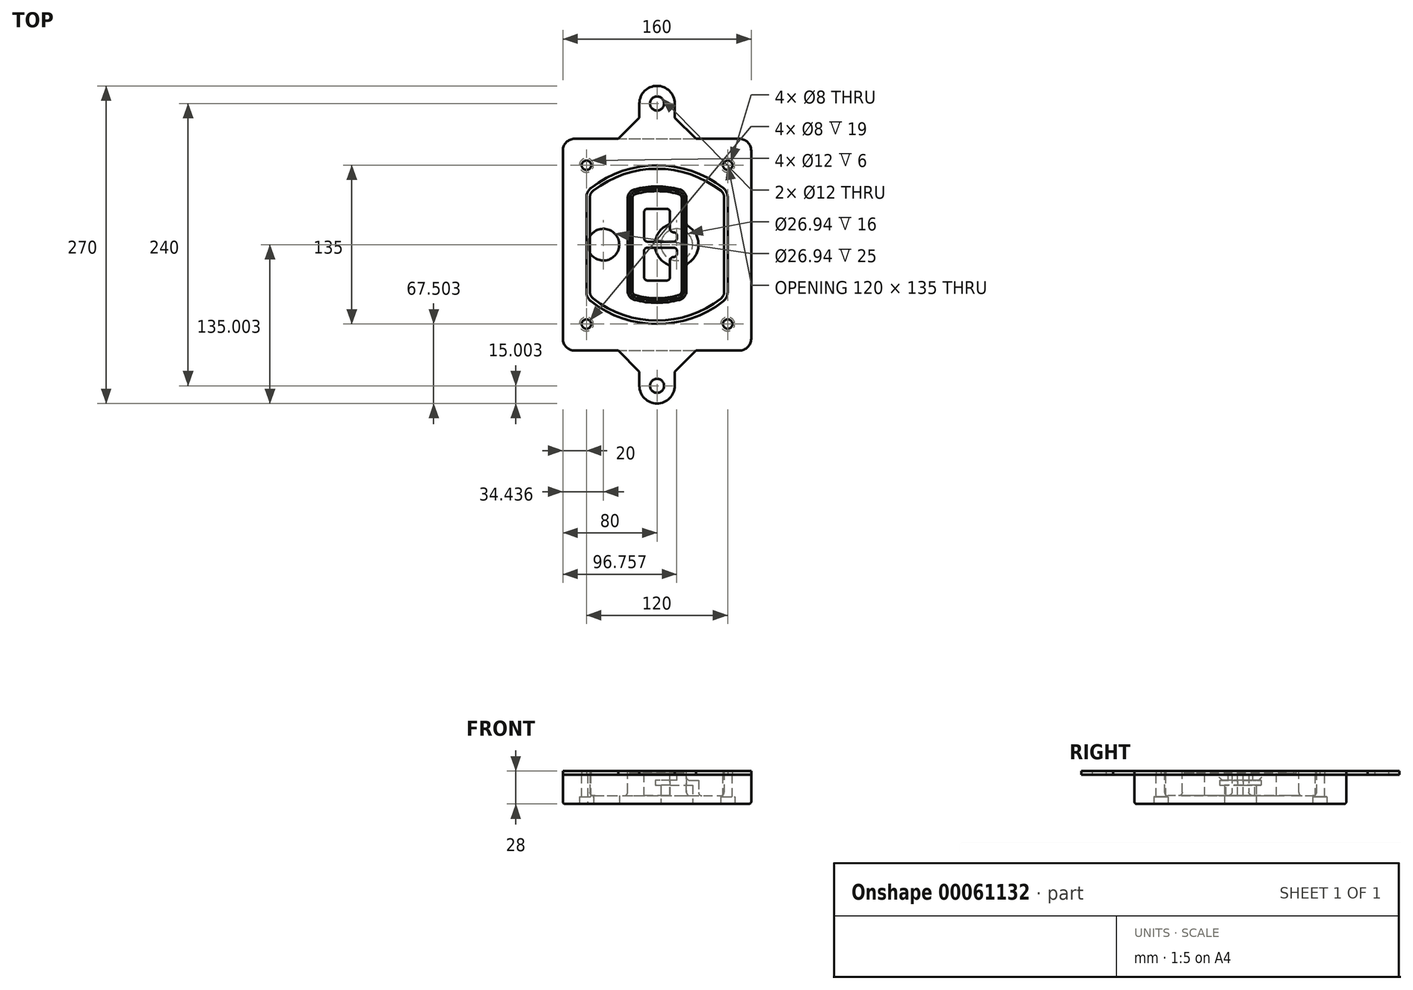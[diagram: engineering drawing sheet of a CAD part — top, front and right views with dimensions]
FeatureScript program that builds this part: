
annotation { "Feature Type Name" : "Feature", "Feature Type Description" : "" }
export const myFeature = defineFeature(function(context is Context, id is Id, definition is map)
    precondition{}
    {
        {
            var Q0;
            Q0=qCreatedBy(makeId("Top.planeOp"),FACE);
            var sketch = newSketch(context, id + "F0", { "sketchPlane" : qUnion([Q0])});
            skPoint(sketch, "E0.rect.middle", {"position": v(0, 0) * mm});
            skLineSegment(sketch, "E1.bottom", {"start": v(24.05, 28.38) * mm, "end": v(164.05, 28.38) * mm});
            skLineSegment(sketch, "E1.top", {"start": v(24.05, 208.38) * mm, "end": v(164.05, 208.38) * mm});
            skLineSegment(sketch, "E1.left", {"start": v(14.05, 38.38) * mm, "end": v(14.05, 198.38) * mm});
            skLineSegment(sketch, "E1.right", {"start": v(174.05, 38.38) * mm, "end": v(174.05, 198.38) * mm});
            skLineSegment(sketch, "E2", {"start": v(14.05, 208.38) * mm, "end": v(174.05, 28.38) * mm, "construction": true});
            skLineSegment(sketch, "E3", {"start": v(174.05, 208.38) * mm, "end": v(14.05, 28.38) * mm, "construction": true});
            skCircle(sketch, "E4", {"center": v(34.05, 185.88) * mm, "radius": 4 * mm});
            skCircle(sketch, "E5", {"center": v(154.05, 185.88) * mm, "radius": 4 * mm});
            skCircle(sketch, "E6", {"center": v(154.05, 50.88) * mm, "radius": 4 * mm});
            skCircle(sketch, "E7", {"center": v(34.05, 50.88) * mm, "radius": 4 * mm});
            skLineSegment(sketch, "E8", {"start": v(34.05, 185.88) * mm, "end": v(154.05, 185.88) * mm, "construction": true});
            skLineSegment(sketch, "E9", {"start": v(154.05, 185.88) * mm, "end": v(154.05, 50.88) * mm, "construction": true});
            skLineSegment(sketch, "E10", {"start": v(154.05, 50.88) * mm, "end": v(34.05, 50.88) * mm, "construction": true});
            skLineSegment(sketch, "E11", {"start": v(34.05, 50.88) * mm, "end": v(34.05, 185.88) * mm, "construction": true});
            skLineSegment(sketch, "E12", {"start": v(34.05, 158.68) * mm, "end": v(34.05, 78.09) * mm});
            skLineSegment(sketch, "E13", {"start": v(154.05, 158.68) * mm, "end": v(154.05, 78.09) * mm});
            skArc(sketch, "E14", {"start": v(150.2, 166.56) * mm, "mid": v(94.05, 185.88) * mm, "end": v(37.9, 166.56) * mm});
            skArc(sketch, "E15", {"start": v(37.9, 70.2) * mm, "mid": v(94.05, 50.88) * mm, "end": v(150.2, 70.2) * mm});
            skLineSegment(sketch, "E16", {"start": v(34.05, 118.38) * mm, "end": v(154.05, 118.38) * mm, "construction": true});
            skPoint(sketch, "E17.visualSharp", {"position": v(34.05, 73.38) * mm});
            skArc(sketch, "E17.filletArc", {"start": v(34.05, 78.09) * mm, "mid": v(35.06, 73.7) * mm, "end": v(37.9, 70.2) * mm});
            skPoint(sketch, "E18.visualSharp", {"position": v(34.05, 163.38) * mm});
            skArc(sketch, "E18.filletArc", {"start": v(37.9, 166.56) * mm, "mid": v(35.06, 163.06) * mm, "end": v(34.05, 158.68) * mm});
            skPoint(sketch, "E19.visualSharp", {"position": v(154.05, 163.38) * mm});
            skArc(sketch, "E19.filletArc", {"start": v(154.05, 158.68) * mm, "mid": v(153.04, 163.06) * mm, "end": v(150.2, 166.56) * mm});
            skPoint(sketch, "E20.visualSharp", {"position": v(154.05, 73.38) * mm});
            skArc(sketch, "E20.filletArc", {"start": v(150.2, 70.2) * mm, "mid": v(153.04, 73.7) * mm, "end": v(154.05, 78.09) * mm});
            skPoint(sketch, "E21.visualSharp", {"position": v(14.05, 208.38) * mm});
            skArc(sketch, "E21.filletArc", {"start": v(24.05, 208.38) * mm, "mid": v(16.98, 205.45) * mm, "end": v(14.05, 198.38) * mm});
            skPoint(sketch, "E22.visualSharp", {"position": v(174.05, 208.38) * mm});
            skArc(sketch, "E22.filletArc", {"start": v(174.05, 198.38) * mm, "mid": v(171.12, 205.45) * mm, "end": v(164.05, 208.38) * mm});
            skPoint(sketch, "E23.visualSharp", {"position": v(174.05, 28.38) * mm});
            skArc(sketch, "E23.filletArc", {"start": v(164.05, 28.38) * mm, "mid": v(171.12, 31.31) * mm, "end": v(174.05, 38.38) * mm});
            skPoint(sketch, "E24.visualSharp", {"position": v(14.05, 28.38) * mm});
            skArc(sketch, "E24.filletArc", {"start": v(14.05, 38.38) * mm, "mid": v(16.98, 31.31) * mm, "end": v(24.05, 28.38) * mm});
            skArc(sketch, "E25.0", {"start": v(151.05, 158.68) * mm, "mid": v(150.34, 161.75) * mm, "end": v(148.36, 164.2) * mm});
            skLineSegment(sketch, "E25.1", {"start": v(151.05, 158.68) * mm, "end": v(151.05, 78.09) * mm});
            skArc(sketch, "E25.2", {"start": v(148.36, 72.57) * mm, "mid": v(150.34, 75.02) * mm, "end": v(151.05, 78.09) * mm});
            skArc(sketch, "E25.3", {"start": v(39.74, 72.57) * mm, "mid": v(94.05, 53.88) * mm, "end": v(148.36, 72.57) * mm});
            skArc(sketch, "E25.4", {"start": v(37.05, 78.09) * mm, "mid": v(37.76, 75.02) * mm, "end": v(39.74, 72.57) * mm});
            skArc(sketch, "E25.5", {"start": v(148.36, 164.2) * mm, "mid": v(94.05, 182.88) * mm, "end": v(39.74, 164.2) * mm});
            skLineSegment(sketch, "E25.6", {"start": v(37.05, 158.68) * mm, "end": v(37.05, 78.09) * mm});
            skArc(sketch, "E25.7", {"start": v(39.74, 164.2) * mm, "mid": v(37.76, 161.75) * mm, "end": v(37.05, 158.68) * mm});
            skArc(sketch, "E26.0", {"start": v(35.43, 169.71) * mm, "mid": v(31.47, 164.82) * mm, "end": v(30.05, 158.68) * mm});
            skArc(sketch, "E26.1", {"start": v(152.67, 169.71) * mm, "mid": v(94.05, 189.88) * mm, "end": v(35.43, 169.71) * mm});
            skArc(sketch, "E26.2", {"start": v(158.05, 158.68) * mm, "mid": v(156.63, 164.82) * mm, "end": v(152.67, 169.71) * mm});
            skLineSegment(sketch, "E26.3", {"start": v(158.05, 158.68) * mm, "end": v(158.05, 78.09) * mm});
            skArc(sketch, "E26.4", {"start": v(152.67, 67.05) * mm, "mid": v(156.63, 71.95) * mm, "end": v(158.05, 78.09) * mm});
            skLineSegment(sketch, "E26.5", {"start": v(30.05, 158.68) * mm, "end": v(30.05, 78.09) * mm});
            skArc(sketch, "E26.6", {"start": v(35.43, 67.05) * mm, "mid": v(94.05, 46.88) * mm, "end": v(152.67, 67.05) * mm});
            skArc(sketch, "E26.7", {"start": v(30.05, 78.09) * mm, "mid": v(31.47, 71.95) * mm, "end": v(35.43, 67.05) * mm});
            skSolve(sketch);
        }
        {
            var Q0;
            Q0=makeQuery(id+"F0.imprint","IMPRINT",FACE,{"disambiguationData":[TD([[makeQuery(id+"F0.imprint","IMPRINT",EDGE,{"derivedFrom":sQuery(id+"F0.wireOp",EDGE,"E1.bottom")}),1.0]])]});
            var Q1;
            Q1=makeQuery(id+"F0.imprint","IMPRINT",FACE,{"disambiguationData":[TD([[makeQuery(id+"F0.imprint","IMPRINT",EDGE,{"derivedFrom":sQuery(id+"F0.wireOp",EDGE,"E12")}),1.0]])]});
            var Q2;
            Q2=makeQuery(id+"F0.imprint","IMPRINT",FACE,{"disambiguationData":[TD([[makeQuery(id+"F0.imprint","IMPRINT",EDGE,{"derivedFrom":sQuery(id+"F0.wireOp",EDGE,"E25.0")}),1.0]])]});
            var Q3;
            Q3=makeQuery(id+"F0.imprint","IMPRINT",FACE,{"disambiguationData":[TD([[makeQuery(id+"F0.imprint","IMPRINT",EDGE,{"derivedFrom":sQuery(id+"F0.wireOp",EDGE,"E12")}),-1.0]])]});
            extrude(context, id + "F1", {"entities" : qUnion([Q0, Q1, Q2, Q3]), "oppositeDirection" : true, "depth" : 25 * mm});
        }
        {
            var Q0;
            Q0=makeQuery(id+"F0.imprint","IMPRINT",FACE,{"disambiguationData":[TD([[makeQuery(id+"F0.imprint","IMPRINT",EDGE,{"derivedFrom":sQuery(id+"F0.wireOp",EDGE,"E12")}),1.0]])]});
            extrude(context, id + "F2", {"entities" : qUnion([Q0]), "operationType" : NewBodyOperationType.ADD, "depth" : 3 * mm});
        }
        {
            var Q0;
            Q0=makeQuery(id+"F0.imprint","IMPRINT",FACE,{"disambiguationData":[TD([[makeQuery(id+"F0.imprint","IMPRINT",EDGE,{"derivedFrom":sQuery(id+"F0.wireOp",EDGE,"E25.0")}),1.0]])]});
            extrude(context, id + "F3", {"entities" : qUnion([Q0]), "operationType" : NewBodyOperationType.REMOVE, "oppositeDirection" : true, "depth" : 18 * mm});
        }
        {
            var Q0;
            Q0=makeQuery(id+"F2.opExtrude","CAP_FACE",FACE,{"disambiguationData":[OSD([sQuery(id+"F0.wireOp",EDGE,"E12"),sQuery(id+"F0.wireOp",EDGE,"E13"),sQuery(id+"F0.wireOp",EDGE,"E14"),sQuery(id+"F0.wireOp",EDGE,"E15"),sQuery(id+"F0.wireOp",EDGE,"E17.filletArc"),sQuery(id+"F0.wireOp",EDGE,"E18.filletArc"),sQuery(id+"F0.wireOp",EDGE,"E19.filletArc"),sQuery(id+"F0.wireOp",EDGE,"E20.filletArc"),sQuery(id+"F0.wireOp",EDGE,"E25.0"),sQuery(id+"F0.wireOp",EDGE,"E25.1"),sQuery(id+"F0.wireOp",EDGE,"E25.2"),sQuery(id+"F0.wireOp",EDGE,"E25.3"),sQuery(id+"F0.wireOp",EDGE,"E25.4"),sQuery(id+"F0.wireOp",EDGE,"E25.5"),sQuery(id+"F0.wireOp",EDGE,"E25.6"),sQuery(id+"F0.wireOp",EDGE,"E25.7")])],"isStart":false});
            var sketch = newSketch(context, id + "F4", { "sketchPlane" : qUnion([Q0])});
            skArc(sketch, "E27.0", {"start": v(74.97, 71.41) * mm, "mid": v(94.05, 68.88) * mm, "end": v(113.13, 71.41) * mm});
            skArc(sketch, "E28.0", {"start": v(113.13, 165.35) * mm, "mid": v(94.05, 167.88) * mm, "end": v(74.97, 165.35) * mm});
            skLineSegment(sketch, "E29", {"start": v(69.05, 157.63) * mm, "end": v(69.05, 79.14) * mm});
            skLineSegment(sketch, "E30", {"start": v(119.05, 157.63) * mm, "end": v(119.05, 79.14) * mm});
            skLineSegment(sketch, "E31", {"start": v(69.05, 163.48) * mm, "end": v(119.05, 163.48) * mm, "construction": true});
            skLineSegment(sketch, "E32", {"start": v(69.05, 73.28) * mm, "end": v(119.05, 73.28) * mm, "construction": true});
            skPoint(sketch, "E33.visualSharp", {"position": v(69.05, 163.48) * mm});
            skArc(sketch, "E33.filletArc", {"start": v(74.97, 165.35) * mm, "mid": v(70.7, 162.5) * mm, "end": v(69.05, 157.63) * mm});
            skPoint(sketch, "E34.visualSharp", {"position": v(119.05, 163.48) * mm});
            skArc(sketch, "E34.filletArc", {"start": v(119.05, 157.63) * mm, "mid": v(117.4, 162.5) * mm, "end": v(113.13, 165.35) * mm});
            skPoint(sketch, "E35.visualSharp", {"position": v(119.05, 73.28) * mm});
            skArc(sketch, "E35.filletArc", {"start": v(113.13, 71.41) * mm, "mid": v(117.4, 74.27) * mm, "end": v(119.05, 79.14) * mm});
            skPoint(sketch, "E36.visualSharp", {"position": v(69.05, 73.28) * mm});
            skArc(sketch, "E36.filletArc", {"start": v(69.05, 79.14) * mm, "mid": v(70.7, 74.27) * mm, "end": v(74.97, 71.41) * mm});
            skArc(sketch, "E37.0", {"start": v(148.36, 164.2) * mm, "mid": v(94.05, 182.88) * mm, "end": v(39.74, 164.2) * mm});
            skArc(sketch, "E37.1", {"start": v(39.74, 164.2) * mm, "mid": v(37.76, 161.75) * mm, "end": v(37.05, 158.68) * mm});
            skLineSegment(sketch, "E37.2", {"start": v(37.05, 158.68) * mm, "end": v(37.05, 78.09) * mm});
            skArc(sketch, "E37.3", {"start": v(37.05, 78.09) * mm, "mid": v(37.76, 75.02) * mm, "end": v(39.74, 72.57) * mm});
            skArc(sketch, "E37.4", {"start": v(39.74, 72.57) * mm, "mid": v(94.05, 53.88) * mm, "end": v(148.36, 72.57) * mm});
            skArc(sketch, "E37.5", {"start": v(148.36, 72.57) * mm, "mid": v(150.34, 75.02) * mm, "end": v(151.05, 78.09) * mm});
            skLineSegment(sketch, "E37.6", {"start": v(151.05, 158.68) * mm, "end": v(151.05, 78.09) * mm});
            skArc(sketch, "E37.7", {"start": v(151.05, 158.68) * mm, "mid": v(150.34, 161.75) * mm, "end": v(148.36, 164.2) * mm});
            skLineSegment(sketch, "E38.0", {"start": v(117.05, 157.63) * mm, "end": v(117.05, 79.14) * mm});
            skArc(sketch, "E38.1", {"start": v(112.61, 73.34) * mm, "mid": v(115.81, 75.49) * mm, "end": v(117.05, 79.14) * mm});
            skArc(sketch, "E38.2", {"start": v(75.49, 73.34) * mm, "mid": v(94.05, 70.88) * mm, "end": v(112.61, 73.34) * mm});
            skArc(sketch, "E38.3", {"start": v(71.05, 79.14) * mm, "mid": v(72.29, 75.49) * mm, "end": v(75.49, 73.34) * mm});
            skLineSegment(sketch, "E38.4", {"start": v(71.05, 157.63) * mm, "end": v(71.05, 79.14) * mm});
            skArc(sketch, "E38.5", {"start": v(117.05, 157.63) * mm, "mid": v(115.81, 161.28) * mm, "end": v(112.61, 163.42) * mm});
            skArc(sketch, "E38.6", {"start": v(75.49, 163.42) * mm, "mid": v(72.29, 161.28) * mm, "end": v(71.05, 157.63) * mm});
            skArc(sketch, "E38.7", {"start": v(112.61, 163.42) * mm, "mid": v(94.05, 165.88) * mm, "end": v(75.49, 163.42) * mm});
            skArc(sketch, "E39.0", {"start": v(115.05, 157.63) * mm, "mid": v(114.23, 160.06) * mm, "end": v(112.1, 161.5) * mm});
            skLineSegment(sketch, "E39.1", {"start": v(115.05, 157.63) * mm, "end": v(115.05, 79.14) * mm});
            skArc(sketch, "E39.2", {"start": v(112.1, 75.27) * mm, "mid": v(114.23, 76.7) * mm, "end": v(115.05, 79.14) * mm});
            skArc(sketch, "E39.3", {"start": v(76, 75.27) * mm, "mid": v(94.05, 72.88) * mm, "end": v(112.1, 75.27) * mm});
            skArc(sketch, "E39.4", {"start": v(73.05, 79.14) * mm, "mid": v(73.87, 76.7) * mm, "end": v(76, 75.27) * mm});
            skArc(sketch, "E39.5", {"start": v(112.1, 161.5) * mm, "mid": v(94.05, 163.88) * mm, "end": v(76, 161.5) * mm});
            skLineSegment(sketch, "E39.6", {"start": v(73.05, 157.63) * mm, "end": v(73.05, 79.14) * mm});
            skArc(sketch, "E39.7", {"start": v(76, 161.5) * mm, "mid": v(73.87, 160.06) * mm, "end": v(73.05, 157.63) * mm});
            skLineSegment(sketch, "E40", {"start": v(69.05, 118.38) * mm, "end": v(119.05, 118.38) * mm, "construction": true});
            skLineSegment(sketch, "E41", {"start": v(83.05, 123.88) * mm, "end": v(83.05, 145.88) * mm});
            skLineSegment(sketch, "E42", {"start": v(86.05, 148.88) * mm, "end": v(102.05, 148.88) * mm});
            skLineSegment(sketch, "E43", {"start": v(105.05, 145.88) * mm, "end": v(105.05, 131.88) * mm});
            skLineSegment(sketch, "E44", {"start": v(108.05, 128.88) * mm, "end": v(108.05, 128.88) * mm});
            skLineSegment(sketch, "E45", {"start": v(111.05, 125.88) * mm, "end": v(111.05, 123.88) * mm});
            skLineSegment(sketch, "E46", {"start": v(108.05, 120.88) * mm, "end": v(86.05, 120.88) * mm});
            skPoint(sketch, "E47.visualSharp", {"position": v(83.05, 148.88) * mm});
            skArc(sketch, "E47.filletArc", {"start": v(86.05, 148.88) * mm, "mid": v(83.93, 148) * mm, "end": v(83.05, 145.88) * mm});
            skPoint(sketch, "E48.visualSharp", {"position": v(105.05, 148.88) * mm});
            skArc(sketch, "E48.filletArc", {"start": v(105.05, 145.88) * mm, "mid": v(104.17, 148) * mm, "end": v(102.05, 148.88) * mm});
            skPoint(sketch, "E49.visualSharp", {"position": v(105.05, 128.88) * mm});
            skArc(sketch, "E49.filletArc", {"start": v(105.05, 131.88) * mm, "mid": v(105.93, 129.76) * mm, "end": v(108.05, 128.88) * mm});
            skPoint(sketch, "E50.visualSharp", {"position": v(111.05, 128.88) * mm});
            skArc(sketch, "E50.filletArc", {"start": v(111.05, 125.88) * mm, "mid": v(110.17, 128) * mm, "end": v(108.05, 128.88) * mm});
            skPoint(sketch, "E51.visualSharp", {"position": v(111.05, 120.88) * mm});
            skArc(sketch, "E51.filletArc", {"start": v(108.05, 120.88) * mm, "mid": v(110.17, 121.76) * mm, "end": v(111.05, 123.88) * mm});
            skPoint(sketch, "E52.visualSharp", {"position": v(83.05, 120.88) * mm});
            skArc(sketch, "E52.filletArc", {"start": v(83.05, 123.88) * mm, "mid": v(83.93, 121.76) * mm, "end": v(86.05, 120.88) * mm});
            skLineSegment(sketch, "E53.0.MirrorCS", {"start": v(108.05, 115.88) * mm, "end": v(86.05, 115.88) * mm});
            skArc(sketch, "E54.0.MirrorCS", {"start": v(83.05, 112.88) * mm, "mid": v(83.93, 115) * mm, "end": v(86.05, 115.88) * mm});
            skLineSegment(sketch, "E55.0.MirrorCS", {"start": v(83.05, 112.88) * mm, "end": v(83.05, 90.88) * mm});
            skArc(sketch, "E56.0.MirrorCS", {"start": v(86.05, 87.88) * mm, "mid": v(83.93, 88.76) * mm, "end": v(83.05, 90.88) * mm});
            skLineSegment(sketch, "E57.0.MirrorCS", {"start": v(86.05, 87.88) * mm, "end": v(102.05, 87.88) * mm});
            skArc(sketch, "E58.0.MirrorCS", {"start": v(105.05, 90.88) * mm, "mid": v(104.17, 88.76) * mm, "end": v(102.05, 87.88) * mm});
            skLineSegment(sketch, "E59.0.MirrorCS", {"start": v(105.05, 90.88) * mm, "end": v(105.05, 104.88) * mm});
            skArc(sketch, "E60.0.MirrorCS", {"start": v(105.05, 104.88) * mm, "mid": v(105.93, 107) * mm, "end": v(108.05, 107.88) * mm});
            skArc(sketch, "E61.0.MirrorCS", {"start": v(111.05, 110.88) * mm, "mid": v(110.17, 108.76) * mm, "end": v(108.05, 107.88) * mm});
            skLineSegment(sketch, "E62.0.MirrorCS", {"start": v(111.05, 110.88) * mm, "end": v(111.05, 112.88) * mm});
            skArc(sketch, "E63.0.MirrorCS", {"start": v(108.05, 115.88) * mm, "mid": v(110.17, 115) * mm, "end": v(111.05, 112.88) * mm});
            skSolve(sketch);
        }
        {
            var Q0;
            Q0=makeQuery(id+"F4.imprint","IMPRINT",FACE,{"disambiguationData":[TD([[makeQuery(id+"F4.imprint","IMPRINT",EDGE,{"derivedFrom":sQuery(id+"F4.wireOp",EDGE,"E27.0")}),1.0]])]});
            var Q1;
            Q1=makeQuery(id+"F4.imprint","IMPRINT",FACE,{"disambiguationData":[TD([[makeQuery(id+"F4.imprint","IMPRINT",EDGE,{"derivedFrom":sQuery(id+"F4.wireOp",EDGE,"E38.0")}),-1.0]])]});
            var Q2;
            Q2=makeQuery(id+"F4.imprint","IMPRINT",FACE,{"disambiguationData":[TD([[makeQuery(id+"F4.imprint","IMPRINT",EDGE,{"derivedFrom":sQuery(id+"F4.wireOp",EDGE,"E39.0")}),1.0]])]});
            extrude(context, id + "F5", {"entities" : qUnion([Q0, Q1, Q2]), "operationType" : NewBodyOperationType.ADD, "endBound" : BoundingType.UP_TO_NEXT, "oppositeDirection" : true, "depth" : 25 * mm});
        }
        {
            var Q0;
            Q0=makeQuery(id+"F4.imprint","IMPRINT",FACE,{"disambiguationData":[TD([[makeQuery(id+"F4.imprint","IMPRINT",EDGE,{"derivedFrom":sQuery(id+"F4.wireOp",EDGE,"E38.0")}),-1.0]])]});
            extrude(context, id + "F6", {"entities" : qUnion([Q0]), "operationType" : NewBodyOperationType.REMOVE, "oppositeDirection" : true, "depth" : 2 * mm});
        }
        {
            var Q0;
            Q0=makeQuery(id+"F1.opExtrude","CAP_FACE",FACE,{"disambiguationData":[OSD([sQuery(id+"F0.wireOp",EDGE,"E1.bottom"),sQuery(id+"F0.wireOp",EDGE,"E1.top"),sQuery(id+"F0.wireOp",EDGE,"E1.left"),sQuery(id+"F0.wireOp",EDGE,"E1.right"),sQuery(id+"F0.wireOp",EDGE,"E4"),sQuery(id+"F0.wireOp",EDGE,"E5"),sQuery(id+"F0.wireOp",EDGE,"E6"),sQuery(id+"F0.wireOp",EDGE,"E7"),sQuery(id+"F0.wireOp",EDGE,"E21.filletArc"),sQuery(id+"F0.wireOp",EDGE,"E22.filletArc"),sQuery(id+"F0.wireOp",EDGE,"E23.filletArc"),sQuery(id+"F0.wireOp",EDGE,"E24.filletArc")])],"isStart":false});
            var sketch = newSketch(context, id + "F7", { "sketchPlane" : qUnion([Q0])});
            skCircle(sketch, "E64", {"center": v(110.8, -118.38) * mm, "radius": 13.47 * mm});
            skCircle(sketch, "E65", {"center": v(48.49, -118.38) * mm, "radius": 13.47 * mm});
            skLineSegment(sketch, "E66", {"start": v(174.05, -118.38) * mm, "end": v(14.05, -118.38) * mm});
            skCircle(sketch, "E67", {"center": v(110.8, -118.38) * mm, "radius": 18.47 * mm});
            skCircle(sketch, "E68", {"center": v(154.05, -185.88) * mm, "radius": 6 * mm});
            skCircle(sketch, "E69", {"center": v(34.05, -185.88) * mm, "radius": 6 * mm});
            skCircle(sketch, "E70", {"center": v(34.05, -50.88) * mm, "radius": 6 * mm});
            skCircle(sketch, "E71", {"center": v(154.05, -50.88) * mm, "radius": 6 * mm});
            skSolve(sketch);
        }
        {
            var Q0;
            {var subQ1=sQuery(id+"F7.wireOp",EDGE,"E66");var subQ4=sQuery(id+"F7.wireOp",EDGE,"E64");var subQ6=makeQuery(id+"F7.imprint","INTERSECT",VERTEX,{"disambiguationData":[OD(0.0)],"derivedFrom":[subQ4,subQ1]});Q0=makeQuery(id+"F7.imprint","IMPRINT",FACE,{"disambiguationData":[TD([[makeQuery(id+"F7.imprint","IMPRINT",EDGE,{"disambiguationData":[TD([[subQ6,-1.0]])],"derivedFrom":subQ4}),-1.0]])]});}
            var Q1;
            {var subQ0=sQuery(id+"F7.wireOp",EDGE,"E66");var subQ1=sQuery(id+"F7.wireOp",EDGE,"E64");var subQ3=makeQuery(id+"F7.imprint","INTERSECT",VERTEX,{"disambiguationData":[OD(0.0)],"derivedFrom":[subQ1,subQ0]});Q1=makeQuery(id+"F7.imprint","IMPRINT",FACE,{"disambiguationData":[TD([[makeQuery(id+"F7.imprint","IMPRINT",EDGE,{"disambiguationData":[TD([[subQ3,-1.0]])],"derivedFrom":subQ1}),1.0]])]});}
            var Q2;
            {var subQ0=sQuery(id+"F7.wireOp",EDGE,"E66");var subQ1=sQuery(id+"F7.wireOp",EDGE,"E64");var subQ3=makeQuery(id+"F7.imprint","INTERSECT",VERTEX,{"disambiguationData":[OD(0.0)],"derivedFrom":[subQ1,subQ0]});Q2=makeQuery(id+"F7.imprint","IMPRINT",FACE,{"disambiguationData":[TD([[makeQuery(id+"F7.imprint","IMPRINT",EDGE,{"disambiguationData":[TD([[subQ3,1.0]])],"derivedFrom":subQ1}),1.0]])]});}
            var Q3;
            {var subQ1=sQuery(id+"F7.wireOp",EDGE,"E66");var subQ4=sQuery(id+"F7.wireOp",EDGE,"E64");var subQ6=makeQuery(id+"F7.imprint","INTERSECT",VERTEX,{"disambiguationData":[OD(0.0)],"derivedFrom":[subQ4,subQ1]});Q3=makeQuery(id+"F7.imprint","IMPRINT",FACE,{"disambiguationData":[TD([[makeQuery(id+"F7.imprint","IMPRINT",EDGE,{"disambiguationData":[TD([[subQ6,1.0]])],"derivedFrom":subQ4}),-1.0]])]});}
            extrude(context, id + "F8", {"entities" : qUnion([Q0, Q1, Q2, Q3]), "operationType" : NewBodyOperationType.ADD, "oppositeDirection" : true, "depth" : 20 * mm});
        }
        {
            var Q0;
            {var subQ0=sQuery(id+"F7.wireOp",EDGE,"E66");var subQ1=sQuery(id+"F7.wireOp",EDGE,"E64");var subQ3=makeQuery(id+"F7.imprint","INTERSECT",VERTEX,{"disambiguationData":[OD(0.0)],"derivedFrom":[subQ1,subQ0]});Q0=makeQuery(id+"F7.imprint","IMPRINT",FACE,{"disambiguationData":[TD([[makeQuery(id+"F7.imprint","IMPRINT",EDGE,{"disambiguationData":[TD([[subQ3,-1.0]])],"derivedFrom":subQ1}),1.0]])]});}
            var Q1;
            {var subQ0=sQuery(id+"F7.wireOp",EDGE,"E66");var subQ1=sQuery(id+"F7.wireOp",EDGE,"E64");var subQ3=makeQuery(id+"F7.imprint","INTERSECT",VERTEX,{"disambiguationData":[OD(0.0)],"derivedFrom":[subQ1,subQ0]});Q1=makeQuery(id+"F7.imprint","IMPRINT",FACE,{"disambiguationData":[TD([[makeQuery(id+"F7.imprint","IMPRINT",EDGE,{"disambiguationData":[TD([[subQ3,1.0]])],"derivedFrom":subQ1}),1.0]])]});}
            extrude(context, id + "F9", {"entities" : qUnion([Q0, Q1]), "operationType" : NewBodyOperationType.REMOVE, "oppositeDirection" : true, "depth" : 16 * mm});
        }
        {
            var Q0;
            {var subQ0=sQuery(id+"F7.wireOp",EDGE,"E66");var subQ1=sQuery(id+"F7.wireOp",EDGE,"E65");var subQ3=makeQuery(id+"F7.imprint","INTERSECT",VERTEX,{"disambiguationData":[OD(0.0)],"derivedFrom":[subQ1,subQ0]});Q0=makeQuery(id+"F7.imprint","IMPRINT",FACE,{"disambiguationData":[TD([[makeQuery(id+"F7.imprint","IMPRINT",EDGE,{"disambiguationData":[TD([[subQ3,-1.0]])],"derivedFrom":subQ1}),1.0]])]});}
            var Q1;
            {var subQ0=sQuery(id+"F7.wireOp",EDGE,"E66");var subQ1=sQuery(id+"F7.wireOp",EDGE,"E65");var subQ3=makeQuery(id+"F7.imprint","INTERSECT",VERTEX,{"disambiguationData":[OD(0.0)],"derivedFrom":[subQ1,subQ0]});Q1=makeQuery(id+"F7.imprint","IMPRINT",FACE,{"disambiguationData":[TD([[makeQuery(id+"F7.imprint","IMPRINT",EDGE,{"disambiguationData":[TD([[subQ3,1.0]])],"derivedFrom":subQ1}),1.0]])]});}
            extrude(context, id + "F10", {"entities" : qUnion([Q0, Q1]), "operationType" : NewBodyOperationType.REMOVE, "oppositeDirection" : true, "depth" : 25 * mm});
        }
        {
            var Q0;
            Q0=makeQuery(id+"F7.imprint","IMPRINT",FACE,{"disambiguationData":[TD([[makeQuery(id+"F7.imprint","IMPRINT",EDGE,{"derivedFrom":sQuery(id+"F7.wireOp",EDGE,"E68")}),1.0]])]});
            var Q1;
            Q1=makeQuery(id+"F7.imprint","IMPRINT",FACE,{"disambiguationData":[TD([[makeQuery(id+"F7.imprint","IMPRINT",EDGE,{"derivedFrom":makeQuery(id+"F1.opExtrude","CAP_EDGE",EDGE,{"disambiguationData":[OSD([sQuery(id+"F0.wireOp",EDGE,"E5")])],"isStart":false})}),-1.0]])]});
            var Q2;
            Q2=makeQuery(id+"F7.imprint","IMPRINT",FACE,{"disambiguationData":[TD([[makeQuery(id+"F7.imprint","IMPRINT",EDGE,{"derivedFrom":sQuery(id+"F7.wireOp",EDGE,"E69")}),1.0]])]});
            var Q3;
            Q3=makeQuery(id+"F7.imprint","IMPRINT",FACE,{"disambiguationData":[TD([[makeQuery(id+"F7.imprint","IMPRINT",EDGE,{"derivedFrom":makeQuery(id+"F1.opExtrude","CAP_EDGE",EDGE,{"disambiguationData":[OSD([sQuery(id+"F0.wireOp",EDGE,"E4")])],"isStart":false})}),-1.0]])]});
            var Q4;
            Q4=makeQuery(id+"F7.imprint","IMPRINT",FACE,{"disambiguationData":[TD([[makeQuery(id+"F7.imprint","IMPRINT",EDGE,{"derivedFrom":sQuery(id+"F7.wireOp",EDGE,"E70")}),1.0]])]});
            var Q5;
            Q5=makeQuery(id+"F7.imprint","IMPRINT",FACE,{"disambiguationData":[TD([[makeQuery(id+"F7.imprint","IMPRINT",EDGE,{"derivedFrom":makeQuery(id+"F1.opExtrude","CAP_EDGE",EDGE,{"disambiguationData":[OSD([sQuery(id+"F0.wireOp",EDGE,"E7")])],"isStart":false})}),-1.0]])]});
            var Q6;
            Q6=makeQuery(id+"F7.imprint","IMPRINT",FACE,{"disambiguationData":[TD([[makeQuery(id+"F7.imprint","IMPRINT",EDGE,{"derivedFrom":sQuery(id+"F7.wireOp",EDGE,"E71")}),1.0]])]});
            var Q7;
            Q7=makeQuery(id+"F7.imprint","IMPRINT",FACE,{"disambiguationData":[TD([[makeQuery(id+"F7.imprint","IMPRINT",EDGE,{"derivedFrom":makeQuery(id+"F1.opExtrude","CAP_EDGE",EDGE,{"disambiguationData":[OSD([sQuery(id+"F0.wireOp",EDGE,"E6")])],"isStart":false})}),-1.0]])]});
            extrude(context, id + "F11", {"entities" : qUnion([Q0, Q1, Q2, Q3, Q4, Q5, Q6, Q7]), "operationType" : NewBodyOperationType.REMOVE, "oppositeDirection" : true, "depth" : 6 * mm});
        }
        {
            var Q0;
            Q0=makeQuery(id+"F9.boolean.opBoolean","COPY",FACE,{"derivedFrom":makeQuery(id+"F9.opExtrude","CAP_FACE",FACE,{"disambiguationData":[OSD([sQuery(id+"F7.wireOp",EDGE,"E64")])],"isStart":false})});
            var sketch = newSketch(context, id + "F12", { "sketchPlane" : qUnion([Q0])});
            skArc(sketch, "E72.0", {"start": v(105.05, -100.83) * mm, "mid": v(96.62, -106.56) * mm, "end": v(92.5, -115.88) * mm});
            skArc(sketch, "E72.1", {"start": v(92.5, -120.88) * mm, "mid": v(96.62, -130.2) * mm, "end": v(105.05, -135.93) * mm});
            skLineSegment(sketch, "E73", {"start": v(92.5, -120.88) * mm, "end": v(108.05, -120.88) * mm});
            skLineSegment(sketch, "E74.0", {"start": v(108.05, -115.88) * mm, "end": v(92.5, -115.88) * mm});
            skArc(sketch, "E74.1", {"start": v(108.05, -115.88) * mm, "mid": v(110.17, -115) * mm, "end": v(111.05, -112.88) * mm});
            skLineSegment(sketch, "E74.2", {"start": v(111.05, -110.88) * mm, "end": v(111.05, -112.88) * mm});
            skArc(sketch, "E74.3", {"start": v(111.05, -110.88) * mm, "mid": v(110.17, -108.76) * mm, "end": v(108.05, -107.88) * mm});
            skArc(sketch, "E74.4", {"start": v(105.05, -104.88) * mm, "mid": v(105.93, -107) * mm, "end": v(108.05, -107.88) * mm});
            skLineSegment(sketch, "E74.5", {"start": v(105.05, -100.83) * mm, "end": v(105.05, -104.88) * mm});
            skLineSegment(sketch, "E74.7", {"start": v(108.05, -120.88) * mm, "end": v(92.5, -120.88) * mm});
            skArc(sketch, "E74.8", {"start": v(108.05, -120.88) * mm, "mid": v(110.17, -121.76) * mm, "end": v(111.05, -123.88) * mm});
            skLineSegment(sketch, "E74.9", {"start": v(111.05, -125.88) * mm, "end": v(111.05, -123.88) * mm});
            skArc(sketch, "E74.10", {"start": v(111.05, -125.88) * mm, "mid": v(110.17, -128) * mm, "end": v(108.05, -128.88) * mm});
            skArc(sketch, "E74.11", {"start": v(105.05, -131.88) * mm, "mid": v(105.93, -129.76) * mm, "end": v(108.05, -128.88) * mm});
            skLineSegment(sketch, "E74.12", {"start": v(105.05, -135.93) * mm, "end": v(105.05, -131.88) * mm});
            skPoint(sketch, "E75.orphan", {"position": v(105.05, -145.88) * mm});
            skPoint(sketch, "E76.orphan", {"position": v(86.05, -120.88) * mm});
            skPoint(sketch, "E77.orphan", {"position": v(86.05, -115.88) * mm});
            skPoint(sketch, "E78.orphan", {"position": v(105.05, -90.88) * mm});
            skSolve(sketch);
        }
        {
            var Q0;
            {var subQ7=sQuery(id+"F12.wireOp",EDGE,"E72.0");var subQ14=sQuery(id+"F12.wireOp",EDGE,"E72.1");var subQ16=sQuery(id+"F12.wireOp",EDGE,"E74.1");var subQ18=sQuery(id+"F12.wireOp",EDGE,"E74.8");Q0=qUnion([makeQuery(id+"F12.imprint","IMPRINT",FACE,{"disambiguationData":[TD([[makeQuery(id+"F12.imprint","IMPRINT",EDGE,{"derivedFrom":subQ7}),1.0]])]}),makeQuery(id+"F12.imprint","IMPRINT",FACE,{"disambiguationData":[TD([[makeQuery(id+"F12.imprint","IMPRINT",EDGE,{"derivedFrom":subQ14}),1.0]])]}),makeQuery(id+"F12.imprint","IMPRINT",FACE,{"disambiguationData":[TD([[makeQuery(id+"F12.imprint","IMPRINT",EDGE,{"derivedFrom":subQ16}),1.0]])]}),makeQuery(id+"F12.imprint","IMPRINT",FACE,{"disambiguationData":[TD([[makeQuery(id+"F12.imprint","IMPRINT",EDGE,{"derivedFrom":subQ18}),-1.0]])]})]);}
            var Q1;
            Q1=makeQuery(id+"F5.boolean.opBoolean","SPLIT",FACE,{"disambiguationData":[TD([makeQuery(id+"F5.opExtrude","SWEPT_FACE",FACE,{"disambiguationData":[OSD([sQuery(id+"F4.wireOp",EDGE,"E41")])]})])],"derivedFrom":makeQuery(id+"F3.boolean.opBoolean","COPY",FACE,{"derivedFrom":makeQuery(id+"F3.opExtrude","CAP_FACE",FACE,{"disambiguationData":[OSD([sQuery(id+"F0.wireOp",EDGE,"E25.0"),sQuery(id+"F0.wireOp",EDGE,"E25.1"),sQuery(id+"F0.wireOp",EDGE,"E25.2"),sQuery(id+"F0.wireOp",EDGE,"E25.3"),sQuery(id+"F0.wireOp",EDGE,"E25.4"),sQuery(id+"F0.wireOp",EDGE,"E25.5"),sQuery(id+"F0.wireOp",EDGE,"E25.6"),sQuery(id+"F0.wireOp",EDGE,"E25.7")])],"isStart":false})})});
            extrude(context, id + "F13", {"entities" : qUnion([Q0]), "operationType" : NewBodyOperationType.REMOVE, "endBound" : BoundingType.UP_TO_SURFACE, "endBoundEntityFace" : qUnion([Q1]), "depth" : 25 * mm});
        }
        {
            var Q0;
            Q0=makeQuery(id+"F3.boolean.opBoolean","COPY",EDGE,{"derivedFrom":makeQuery(id+"F3.opExtrude","CAP_EDGE",EDGE,{"disambiguationData":[OSD([sQuery(id+"F0.wireOp",EDGE,"E25.6")])],"isStart":false})});
            var Q1;
            Q1=makeQuery(id+"F8.boolean.opBoolean","INTERSECT",EDGE,{"derivedFrom":[makeQuery(id+"F5.opExtrude","SWEPT_FACE",FACE,{"disambiguationData":[OSD([sQuery(id+"F4.wireOp",EDGE,"E30")])]}),makeQuery(id+"F8.opExtrude","CAP_FACE",FACE,{"disambiguationData":[OSD([sQuery(id+"F7.wireOp",EDGE,"E67")])],"isStart":false})]});
            var Q2;
            Q2=makeQuery(id+"F8.boolean.opBoolean","INTERSECT",EDGE,{"disambiguationData":[OD(1.0)],"derivedFrom":[makeQuery(id+"F5.opExtrude","SWEPT_FACE",FACE,{"disambiguationData":[OSD([sQuery(id+"F4.wireOp",EDGE,"E30")])]}),makeQuery(id+"F8.opExtrude","SWEPT_FACE",FACE,{"disambiguationData":[OSD([sQuery(id+"F7.wireOp",EDGE,"E67")])]})]});
            var Q3;
            {var subQ0=sQuery(id+"F4.wireOp",EDGE,"E30");Q3=makeQuery(id+"F8.boolean.opBoolean","SPLIT",EDGE,{"disambiguationData":[TD([makeQuery(id+"F5.opExtrude","SWEPT_FACE",FACE,{"disambiguationData":[OSD([sQuery(id+"F4.wireOp",EDGE,"E35.filletArc")])]})])],"derivedFrom":makeQuery(id+"F5.opExtrude","CAP_EDGE",EDGE,{"disambiguationData":[OSD([subQ0])],"isStart":false})});}
            var Q4;
            {var subQ0=sQuery(id+"F0.wireOp",EDGE,"E25.7");var subQ1=sQuery(id+"F0.wireOp",EDGE,"E25.1");var subQ2=sQuery(id+"F0.wireOp",EDGE,"E25.6");var subQ3=sQuery(id+"F0.wireOp",EDGE,"E25.5");var subQ4=sQuery(id+"F0.wireOp",EDGE,"E25.4");var subQ5=sQuery(id+"F0.wireOp",EDGE,"E25.0");var subQ6=sQuery(id+"F0.wireOp",EDGE,"E25.2");var subQ7=sQuery(id+"F0.wireOp",EDGE,"E25.3");Q4=makeQuery(id+"F8.boolean.opBoolean","INTERSECT",EDGE,{"derivedFrom":[makeQuery(id+"F5.boolean.opBoolean","SPLIT",FACE,{"disambiguationData":[TD([makeQuery(id+"F2.opExtrude","SWEPT_FACE",FACE,{"disambiguationData":[OSD([subQ5])]})])],"derivedFrom":makeQuery(id+"F3.boolean.opBoolean","COPY",FACE,{"derivedFrom":makeQuery(id+"F3.opExtrude","CAP_FACE",FACE,{"disambiguationData":[OSD([subQ5,subQ1,subQ6,subQ7,subQ4,subQ3,subQ2,subQ0])],"isStart":false})})}),makeQuery(id+"F8.opExtrude","SWEPT_FACE",FACE,{"disambiguationData":[OSD([sQuery(id+"F7.wireOp",EDGE,"E67")])]})]});}
            var Q5;
            Q5=makeQuery(id+"F8.boolean.opBoolean","INTERSECT",EDGE,{"disambiguationData":[OD(0.0)],"derivedFrom":[makeQuery(id+"F5.opExtrude","SWEPT_FACE",FACE,{"disambiguationData":[OSD([sQuery(id+"F4.wireOp",EDGE,"E30")])]}),makeQuery(id+"F8.opExtrude","SWEPT_FACE",FACE,{"disambiguationData":[OSD([sQuery(id+"F7.wireOp",EDGE,"E67")])]})]});
            fillet(context, id + "F14", {"entities" : qUnion([Q0, Q1, Q2, Q3, Q4, Q5]), "radius" : 3 * mm, "tangentPropagation" : true, "allowEdgeOverflow" : false});
        }
        {
            var Q0;
            Q0=makeQuery(id+"F1.opExtrude","CAP_EDGE",EDGE,{"disambiguationData":[OSD([sQuery(id+"F0.wireOp",EDGE,"E1.bottom")])],"isStart":false});
            fillet(context, id + "F15", {"entities" : qUnion([Q0]), "radius" : 2 * mm, "tangentPropagation" : true, "allowEdgeOverflow" : false});
        }
        {
            var Q0;
            {var subQ0=sQuery(id+"F0.wireOp",EDGE,"E22.filletArc");var subQ1=sQuery(id+"F0.wireOp",EDGE,"E7");var subQ2=sQuery(id+"F0.wireOp",EDGE,"E6");var subQ3=sQuery(id+"F0.wireOp",EDGE,"E5");var subQ4=sQuery(id+"F0.wireOp",EDGE,"E4");var subQ5=sQuery(id+"F0.wireOp",EDGE,"E1.bottom");var subQ6=sQuery(id+"F0.wireOp",EDGE,"E21.filletArc");var subQ7=sQuery(id+"F0.wireOp",EDGE,"E1.top");var subQ8=sQuery(id+"F0.wireOp",EDGE,"E1.left");var subQ9=sQuery(id+"F0.wireOp",EDGE,"E1.right");var subQ10=sQuery(id+"F0.wireOp",EDGE,"E23.filletArc");var subQ11=sQuery(id+"F0.wireOp",EDGE,"E24.filletArc");Q0=makeQuery(id+"F2.boolean.opBoolean","SPLIT",FACE,{"disambiguationData":[TD([makeQuery(id+"F1.opExtrude","SWEPT_FACE",FACE,{"disambiguationData":[OSD([subQ5])]})])],"derivedFrom":makeQuery(id+"F1.opExtrude","CAP_FACE",FACE,{"disambiguationData":[OSD([subQ5,subQ7,subQ8,subQ9,subQ4,subQ3,subQ2,subQ1,subQ6,subQ0,subQ10,subQ11])],"isStart":true})});}
            var sketch = newSketch(context, id + "F16", { "sketchPlane" : qUnion([Q0])});
            skLineSegment(sketch, "E79", {"start": v(61.05, 208.38) * mm, "end": v(79.05, 226.38) * mm});
            skLineSegment(sketch, "E80", {"start": v(94.05, 208.38) * mm, "end": v(94.05, 208.38) * mm});
            skLineSegment(sketch, "E81", {"start": v(127.05, 208.38) * mm, "end": v(109.05, 226.38) * mm});
            skLineSegment(sketch, "E82", {"start": v(79.05, 226.38) * mm, "end": v(79.05, 238.38) * mm});
            skLineSegment(sketch, "E83", {"start": v(109.05, 226.38) * mm, "end": v(109.05, 238.38) * mm});
            skLineSegment(sketch, "E84", {"start": v(94.05, 208.38) * mm, "end": v(94.05, 238.38) * mm, "construction": true});
            skCircle(sketch, "E85", {"center": v(94.05, 238.38) * mm, "radius": 6 * mm});
            skArc(sketch, "E86", {"start": v(109.05, 238.38) * mm, "mid": v(94.05, 253.38) * mm, "end": v(79.05, 238.38) * mm});
            skLineSegment(sketch, "E87", {"start": v(79.05, 226.38) * mm, "end": v(79.05, 208.38) * mm, "construction": true});
            skPoint(sketch, "E88", {"position": v(14.05, 118.38) * mm});
            skPoint(sketch, "E89", {"position": v(174.05, 118.38) * mm});
            skLineSegment(sketch, "E90", {"start": v(14.05, 118.38) * mm, "end": v(174.05, 118.38) * mm, "construction": true});
            skLineSegment(sketch, "E91.MirrorCS", {"start": v(61.05, 28.38) * mm, "end": v(79.05, 10.38) * mm});
            skLineSegment(sketch, "E92.MirrorCS", {"start": v(127.05, 28.38) * mm, "end": v(109.05, 10.38) * mm});
            skCircle(sketch, "E93.MirrorC", {"center": v(94.05, -1.62) * mm, "radius": 6 * mm});
            skLineSegment(sketch, "E94.MirrorCS", {"start": v(94.05, 28.38) * mm, "end": v(94.05, -1.62) * mm, "construction": true});
            skLineSegment(sketch, "E95.MirrorCS", {"start": v(79.05, 10.38) * mm, "end": v(79.05, 28.38) * mm, "construction": true});
            skArc(sketch, "E96.MirrorCS", {"start": v(109.05, -1.62) * mm, "mid": v(94.05, -16.62) * mm, "end": v(79.05, -1.62) * mm});
            skLineSegment(sketch, "E97.MirrorCS", {"start": v(79.05, 10.38) * mm, "end": v(79.05, -1.62) * mm});
            skLineSegment(sketch, "E98.MirrorCS", {"start": v(94.05, 28.38) * mm, "end": v(94.05, 28.38) * mm});
            skLineSegment(sketch, "E99.MirrorCS", {"start": v(109.05, 10.38) * mm, "end": v(109.05, -1.62) * mm});
            skSolve(sketch);
        }
        {
            var Q0;
            {var subQ0=sQuery(id+"F16.wireOp",EDGE,"E79");Q0=makeQuery(id+"F16.imprint","IMPRINT",FACE,{"disambiguationData":[TD([[makeQuery(id+"F16.imprint","IMPRINT",EDGE,{"derivedFrom":subQ0}),-1.0]])]});}
            var Q1;
            {var subQ0=sQuery(id+"F16.wireOp",EDGE,"E91.MirrorCS");Q1=makeQuery(id+"F16.imprint","IMPRINT",FACE,{"disambiguationData":[TD([[makeQuery(id+"F16.imprint","IMPRINT",EDGE,{"derivedFrom":subQ0}),1.0]])]});}
            var Q2;
            Q2=makeQuery(id+"F16.imprint","IMPRINT",FACE,{"disambiguationData":[TD([[makeQuery(id+"F16.imprint","IMPRINT",EDGE,{"derivedFrom":makeQuery(id+"F1.opExtrude","CAP_EDGE",EDGE,{"disambiguationData":[OSD([sQuery(id+"F0.wireOp",EDGE,"E1.left")])],"isStart":true})}),-1.0]])]});
            var Q3;
            Q3=makeQuery(id+"F2.opExtrude","CAP_FACE",FACE,{"disambiguationData":[OSD([sQuery(id+"F0.wireOp",EDGE,"E12"),sQuery(id+"F0.wireOp",EDGE,"E13"),sQuery(id+"F0.wireOp",EDGE,"E14"),sQuery(id+"F0.wireOp",EDGE,"E15"),sQuery(id+"F0.wireOp",EDGE,"E17.filletArc"),sQuery(id+"F0.wireOp",EDGE,"E18.filletArc"),sQuery(id+"F0.wireOp",EDGE,"E19.filletArc"),sQuery(id+"F0.wireOp",EDGE,"E20.filletArc"),sQuery(id+"F0.wireOp",EDGE,"E25.0"),sQuery(id+"F0.wireOp",EDGE,"E25.1"),sQuery(id+"F0.wireOp",EDGE,"E25.2"),sQuery(id+"F0.wireOp",EDGE,"E25.3"),sQuery(id+"F0.wireOp",EDGE,"E25.4"),sQuery(id+"F0.wireOp",EDGE,"E25.5"),sQuery(id+"F0.wireOp",EDGE,"E25.6"),sQuery(id+"F0.wireOp",EDGE,"E25.7")])],"isStart":false});
            extrude(context, id + "F17", {"entities" : qUnion([Q0, Q1, Q2]), "endBound" : BoundingType.UP_TO_SURFACE, "endBoundEntityFace" : qUnion([Q3]), "depth" : 25 * mm});
        }
    });
